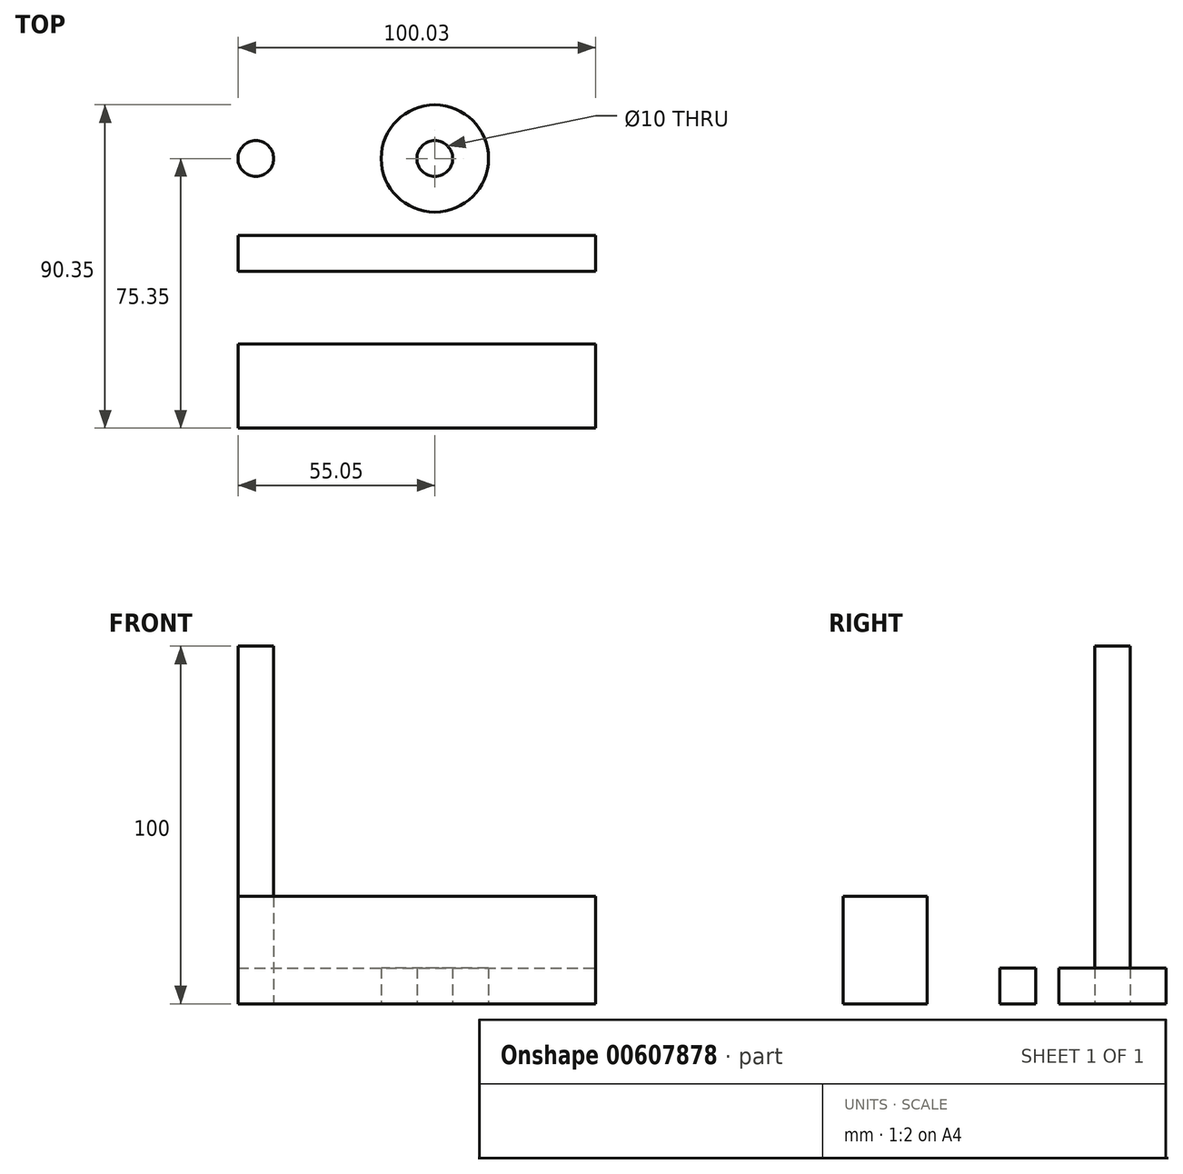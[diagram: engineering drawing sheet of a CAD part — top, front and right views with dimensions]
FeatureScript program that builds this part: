
annotation { "Feature Type Name" : "Feature", "Feature Type Description" : "" }
export const myFeature = defineFeature(function(context is Context, id is Id, definition is map)
    precondition{}
    {
        {
            var Q0;
            Q0=qCreatedBy(makeId("Top.planeOp"),FACE);
            var sketch = newSketch(context, id + "F0", { "sketchPlane" : qUnion([Q0])});
            skCircle(sketch, "E0", {"center": v(0, 0) * mm, "radius": 15 * mm});
            skLineSegment(sketch, "E1.bottom", {"start": v(-55.02, -21.52) * mm, "end": v(44.98, -21.52) * mm});
            skLineSegment(sketch, "E1.top", {"start": v(-55.02, -31.52) * mm, "end": v(44.98, -31.52) * mm});
            skLineSegment(sketch, "E1.left", {"start": v(-55.02, -21.52) * mm, "end": v(-55.02, -31.52) * mm});
            skLineSegment(sketch, "E1.right", {"start": v(44.98, -21.52) * mm, "end": v(44.98, -31.52) * mm});
            skCircle(sketch, "E2", {"center": v(0, 0) * mm, "radius": 5 * mm});
            skCircle(sketch, "E3", {"center": v(-50.05, 0) * mm, "radius": 5 * mm});
            skPoint(sketch, "E4.firstSnap0", {"position": v(-55.02, -26.52) * mm});
            skLineSegment(sketch, "E4.bottom", {"start": v(-55.02, -51.85) * mm, "end": v(44.98, -51.85) * mm});
            skLineSegment(sketch, "E4.top", {"start": v(-55.02, -75.35) * mm, "end": v(44.98, -75.35) * mm});
            skLineSegment(sketch, "E4.left", {"start": v(-55.02, -51.85) * mm, "end": v(-55.02, -75.35) * mm});
            skLineSegment(sketch, "E4.right", {"start": v(44.98, -51.85) * mm, "end": v(44.98, -75.35) * mm});
            skSolve(sketch);
        }
        {
            var Q0;
            Q0=makeQuery(id+"F0.imprint","IMPRINT",FACE,{"disambiguationData":[TD([[makeQuery(id+"F0.imprint","IMPRINT",EDGE,{"derivedFrom":sQuery(id+"F0.wireOp",EDGE,"E0")}),1.0]])]});
            var Q1;
            Q1=makeQuery(id+"F0.imprint","IMPRINT",FACE,{"disambiguationData":[TD([[makeQuery(id+"F0.imprint","IMPRINT",EDGE,{"derivedFrom":sQuery(id+"F0.wireOp",EDGE,"E1.bottom")}),-1.0]])]});
            extrude(context, id + "F1", {"entities" : qUnion([Q0, Q1]), "depth" : 10 * mm, "offsetDistance" : 25 * mm});
        }
        {
            var Q0;
            Q0=makeQuery(id+"F0.imprint","IMPRINT",FACE,{"disambiguationData":[TD([[makeQuery(id+"F0.imprint","IMPRINT",EDGE,{"derivedFrom":sQuery(id+"F0.wireOp",EDGE,"E3")}),1.0]])]});
            extrude(context, id + "F2", {"entities" : qUnion([Q0]), "depth" : 100 * mm, "offsetDistance" : 25 * mm});
        }
        {
            var Q0;
            Q0=makeQuery(id+"F0.imprint","IMPRINT",FACE,{"disambiguationData":[TD([[makeQuery(id+"F0.imprint","IMPRINT",EDGE,{"derivedFrom":sQuery(id+"F0.wireOp",EDGE,"E4.bottom")}),-1.0]])]});
            extrude(context, id + "F3", {"entities" : qUnion([Q0]), "depth" : 30 * mm, "offsetDistance" : 25 * mm});
        }
    });
